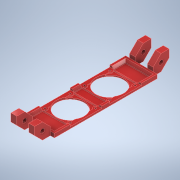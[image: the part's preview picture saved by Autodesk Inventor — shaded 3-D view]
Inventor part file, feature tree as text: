
AUTODESK INVENTOR PART (.ipt)
format: ipt  version: 2021 (Build 250183000, 183)  size: 315,392 bytes
history: native  units: in
note: dims shown in document units (in); Inventor stores cm internally (conversion verified against a paired STEP export)
features: extrude x4, hole x3, other x2, chamfer x1
ambient origin geometry x8: Origin, YZ Plane, XZ Plane, XY Plane, X Axis, Y Axis, Z Axis, Center Point
bodies: Solid1 (feature_tree)
feature tree (10):
  other  "Base Profile"
  extrude  "Base Extrusion"  Depth=0.7874in
  hole  "Fixing Holes"  [1 undecoded]
  other  "Cutouts and Structure"
  extrude  "Structure Subtract"  Depth=5.1181in
  extrude  "Fan Cutout Subtract"  Depth=0.1969in
  hole  "Fan Mounting Holes"  [1 undecoded]
  hole  "Fan Airholes"  [1 undecoded]
  chamfer  "Structure Clearance"  Distance=1.5748in
  extrude  "Extrusion6"  Depth=0.1969in
note: 3 required parameter values undecoded (feature->parameter linkage not recoverable at this tier; creation-order binding heuristic only, values carry confidence <= 0.55)
